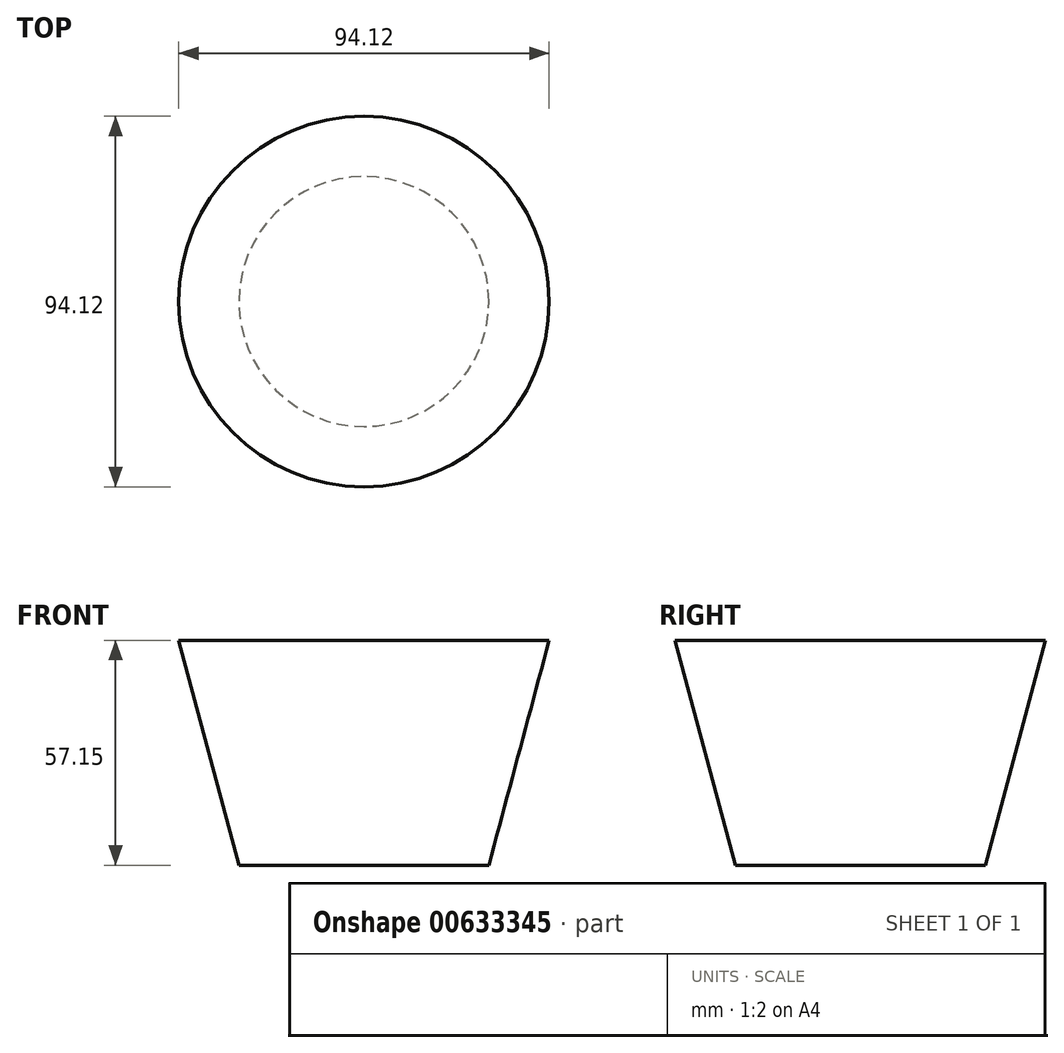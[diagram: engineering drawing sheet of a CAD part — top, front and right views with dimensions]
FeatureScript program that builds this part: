
annotation { "Feature Type Name" : "Feature", "Feature Type Description" : "" }
export const myFeature = defineFeature(function(context is Context, id is Id, definition is map)
    precondition{}
    {
        {
            var Q0;
            Q0=qCreatedBy(makeId("Top.planeOp"),FACE);
            var sketch = newSketch(context, id + "F0", { "sketchPlane" : qUnion([Q0])});
            skCircle(sketch, "E0", {"center": v(0, 0) * mm, "radius": 31.75 * mm});
            skSolve(sketch);
        }
        {
            var Q0;
            Q0=makeQuery(id+"F0.imprint","IMPRINT",FACE,{"disambiguationData":[TD([[makeQuery(id+"F0.imprint","IMPRINT",EDGE,{"derivedFrom":sQuery(id+"F0.wireOp",EDGE,"E0")}),1.0]])]});
            extrude(context, id + "F1", {"entities" : qUnion([Q0]), "depth" : 57.15 * mm, "offsetDistance" : 25.4 * mm, "hasDraft" : true, "draftAngle" : 15 * degree});
        }
    });
